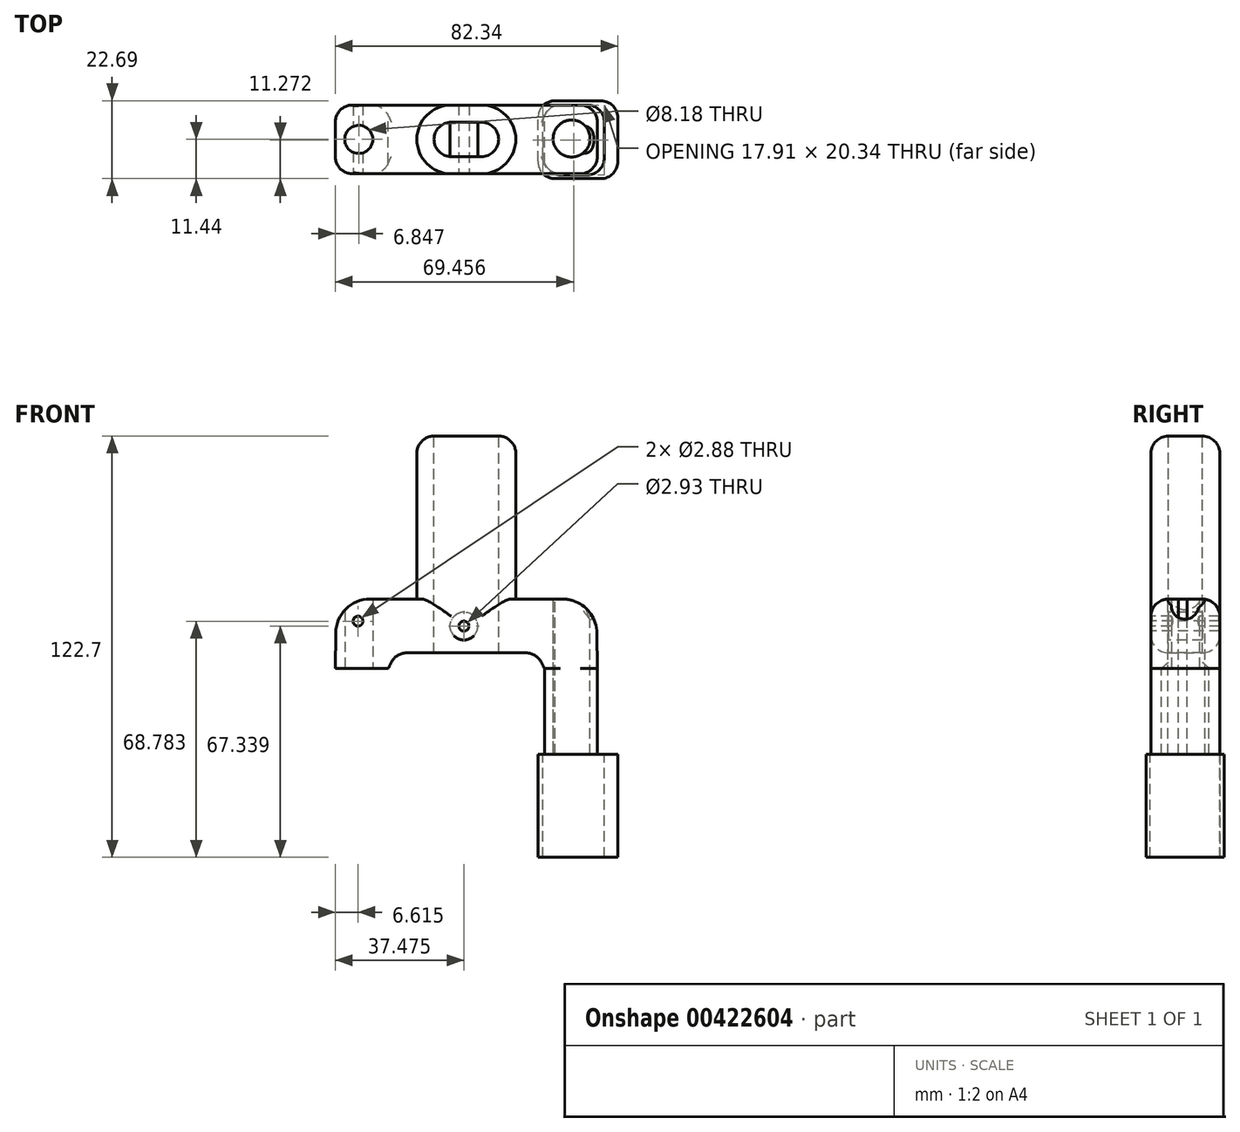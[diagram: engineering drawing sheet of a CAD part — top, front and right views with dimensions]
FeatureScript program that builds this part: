
annotation { "Feature Type Name" : "Feature", "Feature Type Description" : "" }
export const myFeature = defineFeature(function(context is Context, id is Id, definition is map)
    precondition{}
    {
        {
            var Q0;
            Q0=qCreatedBy(makeId("Front.planeOp"),FACE);
            var sketch = newSketch(context, id + "F0", { "sketchPlane" : qUnion([Q0])});
            skLineSegment(sketch, "E0", {"start": v(-67.5, -51.7) * mm, "end": v(-52.08, -51.7) * mm});
            skLineSegment(sketch, "E1", {"start": v(-52.08, -51.7) * mm, "end": v(-49.8, -47.15) * mm});
            skLineSegment(sketch, "E2", {"start": v(-49.8, -47.15) * mm, "end": v(-29.33, -47.15) * mm});
            skLineSegment(sketch, "E3", {"start": v(-29.33, -47.15) * mm, "end": v(-29.33, 0) * mm});
            skLineSegment(sketch, "E4", {"start": v(-29.33, 0) * mm, "end": v(-43.74, 0) * mm});
            skLineSegment(sketch, "E5", {"start": v(-43.74, 0) * mm, "end": v(-43.74, -31.47) * mm});
            skLineSegment(sketch, "E6", {"start": v(-43.74, -31.47) * mm, "end": v(-67.25, -31.47) * mm});
            skLineSegment(sketch, "E7", {"start": v(-67.25, -31.47) * mm, "end": v(-67.5, -51.7) * mm});
            skLineSegment(sketch, "E8.MirrorCS", {"start": v(-6.57, -51.7) * mm, "end": v(-8.85, -47.15) * mm});
            skLineSegment(sketch, "E9.MirrorCS", {"start": v(8.85, -51.7) * mm, "end": v(-6.57, -51.7) * mm});
            skLineSegment(sketch, "E10.MirrorCS", {"start": v(-14.92, -31.47) * mm, "end": v(8.6, -31.47) * mm});
            skLineSegment(sketch, "E11.MirrorCS", {"start": v(8.6, -31.47) * mm, "end": v(8.85, -51.7) * mm});
            skLineSegment(sketch, "E12.MirrorCS", {"start": v(-8.85, -47.15) * mm, "end": v(-29.33, -47.15) * mm});
            skLineSegment(sketch, "E13.MirrorCS", {"start": v(-29.33, 0) * mm, "end": v(-14.92, 0) * mm});
            skLineSegment(sketch, "E14.MirrorCS", {"start": v(-14.92, 0) * mm, "end": v(-14.92, -31.47) * mm});
            skSolve(sketch);
        }
        {
            var Q0;
            Q0=qSketchRegion(id+"F0",true);
            extrude(context, id + "F1", {"entities" : qUnion([Q0]), "depth" : 20 * mm});
        }
        {
            var Q0;
            Q0=makeQuery(id+"F1.opExtrude","SWEPT_EDGE",EDGE,{"disambiguationData":[OSD([sQuery(id+"F0.wireOp",EDGE,"E10.MirrorCS"),sQuery(id+"F0.wireOp",EDGE,"E11.MirrorCS")])]});
            var Q1;
            Q1=makeQuery(id+"F1.opExtrude","SWEPT_EDGE",EDGE,{"disambiguationData":[OSD([sQuery(id+"F0.wireOp",EDGE,"E6"),sQuery(id+"F0.wireOp",EDGE,"E7")])]});
            var Q2;
            Q2=makeQuery(id+"F1.opExtrude","CAP_EDGE",EDGE,{"disambiguationData":[OSD([sQuery(id+"F0.wireOp",EDGE,"E5")])],"isStart":false});
            var Q3;
            Q3=makeQuery(id+"F1.opExtrude","CAP_EDGE",EDGE,{"disambiguationData":[OSD([sQuery(id+"F0.wireOp",EDGE,"E14.MirrorCS")])],"isStart":false});
            var Q4;
            Q4=makeQuery(id+"F1.opExtrude","CAP_EDGE",EDGE,{"disambiguationData":[OSD([sQuery(id+"F0.wireOp",EDGE,"E5")])],"isStart":true});
            var Q5;
            Q5=makeQuery(id+"F1.opExtrude","CAP_EDGE",EDGE,{"disambiguationData":[OSD([sQuery(id+"F0.wireOp",EDGE,"E14.MirrorCS")])],"isStart":true});
            fillet(context, id + "F2", {"entities" : qUnion([Q0, Q1, Q2, Q3, Q4, Q5]), "radius" : 10 * mm, "tangentPropagation" : true, "allowEdgeOverflow" : false});
        }
        {
            var Q0;
            Q0=makeQuery(id+"F1.opExtrude","SWEPT_FACE",FACE,{"disambiguationData":[OSD([sQuery(id+"F0.wireOp",EDGE,"E4"),sQuery(id+"F0.wireOp",EDGE,"E13.MirrorCS")])]});
            extrude(context, id + "F3", {"entities" : qUnion([Q0]), "operationType" : NewBodyOperationType.ADD, "depth" : 16 * mm});
        }
        {
            var Q0;
            Q0=makeQuery(id+"F1.opExtrude","CAP_EDGE",EDGE,{"disambiguationData":[OSD([sQuery(id+"F0.wireOp",EDGE,"E11.MirrorCS")])],"isStart":false});
            var Q1;
            Q1=makeQuery(id+"F1.opExtrude","CAP_EDGE",EDGE,{"disambiguationData":[OSD([sQuery(id+"F0.wireOp",EDGE,"E6")])],"isStart":false});
            var Q2;
            {var subQ0=sQuery(id+"F0.wireOp",EDGE,"E7");var subQ1=sQuery(id+"F0.wireOp",EDGE,"E6");Q2=makeQuery(id+"F2.opFillet","BLEND_EDGE",EDGE,{"blendedFrom":[makeQuery(id+"F1.opExtrude","SWEPT_EDGE",EDGE,{"disambiguationData":[OSD([subQ1,subQ0])]}),makeQuery(id+"F1.opExtrude","CAP_FACE",FACE,{"disambiguationData":[OSD([sQuery(id+"F0.wireOp",EDGE,"E0"),sQuery(id+"F0.wireOp",EDGE,"E1"),sQuery(id+"F0.wireOp",EDGE,"E2"),sQuery(id+"F0.wireOp",EDGE,"E4"),sQuery(id+"F0.wireOp",EDGE,"E5"),subQ1,subQ0,sQuery(id+"F0.wireOp",EDGE,"E8.MirrorCS"),sQuery(id+"F0.wireOp",EDGE,"E9.MirrorCS"),sQuery(id+"F0.wireOp",EDGE,"E10.MirrorCS"),sQuery(id+"F0.wireOp",EDGE,"E11.MirrorCS"),sQuery(id+"F0.wireOp",EDGE,"E12.MirrorCS"),sQuery(id+"F0.wireOp",EDGE,"E13.MirrorCS"),sQuery(id+"F0.wireOp",EDGE,"E14.MirrorCS")])],"isStart":false})],"blendedInto":[makeQuery(id+"F1.opExtrude","CAP_FACE",FACE,{"disambiguationData":[OSD([sQuery(id+"F0.wireOp",EDGE,"E0"),sQuery(id+"F0.wireOp",EDGE,"E1"),sQuery(id+"F0.wireOp",EDGE,"E2"),sQuery(id+"F0.wireOp",EDGE,"E4"),sQuery(id+"F0.wireOp",EDGE,"E5"),subQ1,subQ0,sQuery(id+"F0.wireOp",EDGE,"E8.MirrorCS"),sQuery(id+"F0.wireOp",EDGE,"E9.MirrorCS"),sQuery(id+"F0.wireOp",EDGE,"E10.MirrorCS"),sQuery(id+"F0.wireOp",EDGE,"E11.MirrorCS"),sQuery(id+"F0.wireOp",EDGE,"E12.MirrorCS"),sQuery(id+"F0.wireOp",EDGE,"E13.MirrorCS"),sQuery(id+"F0.wireOp",EDGE,"E14.MirrorCS")])],"isStart":false})]});}
            var Q3;
            {var subQ0=sQuery(id+"F0.wireOp",EDGE,"E11.MirrorCS");var subQ1=sQuery(id+"F0.wireOp",EDGE,"E10.MirrorCS");Q3=makeQuery(id+"F2.opFillet","BLEND_EDGE",EDGE,{"blendedFrom":[makeQuery(id+"F1.opExtrude","SWEPT_EDGE",EDGE,{"disambiguationData":[OSD([subQ1,subQ0])]}),makeQuery(id+"F1.opExtrude","CAP_FACE",FACE,{"disambiguationData":[OSD([sQuery(id+"F0.wireOp",EDGE,"E0"),sQuery(id+"F0.wireOp",EDGE,"E1"),sQuery(id+"F0.wireOp",EDGE,"E2"),sQuery(id+"F0.wireOp",EDGE,"E4"),sQuery(id+"F0.wireOp",EDGE,"E5"),sQuery(id+"F0.wireOp",EDGE,"E6"),sQuery(id+"F0.wireOp",EDGE,"E7"),sQuery(id+"F0.wireOp",EDGE,"E8.MirrorCS"),sQuery(id+"F0.wireOp",EDGE,"E9.MirrorCS"),subQ1,subQ0,sQuery(id+"F0.wireOp",EDGE,"E12.MirrorCS"),sQuery(id+"F0.wireOp",EDGE,"E13.MirrorCS"),sQuery(id+"F0.wireOp",EDGE,"E14.MirrorCS")])],"isStart":true})],"blendedInto":[makeQuery(id+"F1.opExtrude","CAP_FACE",FACE,{"disambiguationData":[OSD([sQuery(id+"F0.wireOp",EDGE,"E0"),sQuery(id+"F0.wireOp",EDGE,"E1"),sQuery(id+"F0.wireOp",EDGE,"E2"),sQuery(id+"F0.wireOp",EDGE,"E4"),sQuery(id+"F0.wireOp",EDGE,"E5"),sQuery(id+"F0.wireOp",EDGE,"E6"),sQuery(id+"F0.wireOp",EDGE,"E7"),sQuery(id+"F0.wireOp",EDGE,"E8.MirrorCS"),sQuery(id+"F0.wireOp",EDGE,"E9.MirrorCS"),subQ1,subQ0,sQuery(id+"F0.wireOp",EDGE,"E12.MirrorCS"),sQuery(id+"F0.wireOp",EDGE,"E13.MirrorCS"),sQuery(id+"F0.wireOp",EDGE,"E14.MirrorCS")])],"isStart":true})]});}
            var Q4;
            {var subQ0=sQuery(id+"F0.wireOp",EDGE,"E7");var subQ1=sQuery(id+"F0.wireOp",EDGE,"E6");Q4=makeQuery(id+"F2.opFillet","BLEND_EDGE",EDGE,{"blendedFrom":[makeQuery(id+"F1.opExtrude","SWEPT_EDGE",EDGE,{"disambiguationData":[OSD([subQ1,subQ0])]}),makeQuery(id+"F1.opExtrude","CAP_FACE",FACE,{"disambiguationData":[OSD([sQuery(id+"F0.wireOp",EDGE,"E0"),sQuery(id+"F0.wireOp",EDGE,"E1"),sQuery(id+"F0.wireOp",EDGE,"E2"),sQuery(id+"F0.wireOp",EDGE,"E4"),sQuery(id+"F0.wireOp",EDGE,"E5"),subQ1,subQ0,sQuery(id+"F0.wireOp",EDGE,"E8.MirrorCS"),sQuery(id+"F0.wireOp",EDGE,"E9.MirrorCS"),sQuery(id+"F0.wireOp",EDGE,"E10.MirrorCS"),sQuery(id+"F0.wireOp",EDGE,"E11.MirrorCS"),sQuery(id+"F0.wireOp",EDGE,"E12.MirrorCS"),sQuery(id+"F0.wireOp",EDGE,"E13.MirrorCS"),sQuery(id+"F0.wireOp",EDGE,"E14.MirrorCS")])],"isStart":true})],"blendedInto":[makeQuery(id+"F1.opExtrude","CAP_FACE",FACE,{"disambiguationData":[OSD([sQuery(id+"F0.wireOp",EDGE,"E0"),sQuery(id+"F0.wireOp",EDGE,"E1"),sQuery(id+"F0.wireOp",EDGE,"E2"),sQuery(id+"F0.wireOp",EDGE,"E4"),sQuery(id+"F0.wireOp",EDGE,"E5"),subQ1,subQ0,sQuery(id+"F0.wireOp",EDGE,"E8.MirrorCS"),sQuery(id+"F0.wireOp",EDGE,"E9.MirrorCS"),sQuery(id+"F0.wireOp",EDGE,"E10.MirrorCS"),sQuery(id+"F0.wireOp",EDGE,"E11.MirrorCS"),sQuery(id+"F0.wireOp",EDGE,"E12.MirrorCS"),sQuery(id+"F0.wireOp",EDGE,"E13.MirrorCS"),sQuery(id+"F0.wireOp",EDGE,"E14.MirrorCS")])],"isStart":true})]});}
            var Q5;
            Q5=makeQuery(id+"F3.opExtrude","CAP_EDGE",EDGE,{"disambiguationData":[OSD([sQuery(id+"F0.wireOp",EDGE,"E4"),sQuery(id+"F0.wireOp",EDGE,"E13.MirrorCS"),sQuery(id+"F0.wireOp",EDGE,"E14.MirrorCS")])],"isStart":false});
            var Q6;
            Q6=makeQuery(id+"F3.opExtrude","CAP_EDGE",EDGE,{"disambiguationData":[OSD([sQuery(id+"F0.wireOp",EDGE,"E4"),sQuery(id+"F0.wireOp",EDGE,"E5"),sQuery(id+"F0.wireOp",EDGE,"E13.MirrorCS")])],"isStart":false});
            var Q7;
            {var subQ0=sQuery(id+"F0.wireOp",EDGE,"E13.MirrorCS");var subQ1=sQuery(id+"F0.wireOp",EDGE,"E4");Q7=makeQuery(id+"F3.opExtrude","CAP_EDGE",EDGE,{"disambiguationData":[OSD([subQ1,subQ0]),TDD([makeQuery(id+"F1.opExtrude","CAP_EDGE",EDGE,{"disambiguationData":[OSD([subQ1,subQ0])],"isStart":false})])],"isStart":false});}
            fillet(context, id + "F4", {"entities" : qUnion([Q0, Q1, Q2, Q3, Q4, Q5, Q6, Q7]), "radius" : 5 * mm, "tangentPropagation" : true, "allowEdgeOverflow" : false});
        }
        {
            var Q0;
            Q0=makeQuery(id+"F1.opExtrude","SWEPT_FACE",FACE,{"disambiguationData":[OSD([sQuery(id+"F0.wireOp",EDGE,"E2"),sQuery(id+"F0.wireOp",EDGE,"E12.MirrorCS")])]});
            fillet(context, id + "F5", {"entities" : qUnion([Q0]), "radius" : 5 * mm, "tangentPropagation" : true, "allowEdgeOverflow" : false});
        }
        {
            var Q0;
            Q0=makeQuery(id+"F3.opExtrude","CAP_FACE",FACE,{"disambiguationData":[OSD([sQuery(id+"F0.wireOp",EDGE,"E4"),sQuery(id+"F0.wireOp",EDGE,"E13.MirrorCS")])],"isStart":false});
            extrude(context, id + "F6", {"entities" : qUnion([Q0]), "operationType" : NewBodyOperationType.REMOVE, "oppositeDirection" : true, "depth" : 89 * mm});
        }
        {
            var Q0;
            Q0=makeQuery(id+"F1.opExtrude","SWEPT_FACE",FACE,{"disambiguationData":[OSD([sQuery(id+"F0.wireOp",EDGE,"E0")])]});
            var sketch = newSketch(context, id + "F7", { "sketchPlane" : qUnion([Q0])});
            skCircle(sketch, "E15", {"center": v(-60.65, 10) * mm, "radius": 4.09 * mm});
            skPoint(sketch, "E15.centerSnap0", {"position": v(-57.67, 10) * mm});
            skSolve(sketch);
        }
        {
            var Q0;
            Q0=makeQuery(id+"F7.imprint","IMPRINT",FACE,{"disambiguationData":[TD([[makeQuery(id+"F7.imprint","IMPRINT",EDGE,{"derivedFrom":sQuery(id+"F7.wireOp",EDGE,"E15")}),1.0]])]});
            var Q1;
            Q1=sQuery(id+"F7.wireOp",EDGE,"E15");
            extrude(context, id + "F8", {"entities" : qUnion([Q0]), "operationType" : NewBodyOperationType.REMOVE, "surfaceEntities" : qUnion([Q1]), "oppositeDirection" : true, "depth" : 25 * mm});
        }
        {
            var Q0;
            Q0=makeQuery(id+"F1.opExtrude","SWEPT_FACE",FACE,{"disambiguationData":[OSD([sQuery(id+"F0.wireOp",EDGE,"E9.MirrorCS")])]});
            var sketch = newSketch(context, id + "F9", { "sketchPlane" : qUnion([Q0])});
            skCircle(sketch, "E16", {"center": v(0, 10) * mm, "radius": 4.07 * mm});
            skPoint(sketch, "E16.centerSnap0", {"position": v(3.85, 10) * mm});
            skSolve(sketch);
        }
        {
            var Q0;
            Q0=makeQuery(id+"F9.imprint","IMPRINT",FACE,{"disambiguationData":[TD([[makeQuery(id+"F9.imprint","IMPRINT",EDGE,{"derivedFrom":sQuery(id+"F9.wireOp",EDGE,"E16")}),1.0]])]});
            extrude(context, id + "F10", {"entities" : qUnion([Q0]), "operationType" : NewBodyOperationType.REMOVE, "oppositeDirection" : true, "depth" : 25 * mm});
        }
        {
            var Q0;
            Q0=makeQuery(id+"F1.opExtrude","SWEPT_FACE",FACE,{"disambiguationData":[OSD([sQuery(id+"F0.wireOp",EDGE,"E9.MirrorCS")])]});
            extrude(context, id + "F11", {"entities" : qUnion([Q0]), "operationType" : NewBodyOperationType.ADD, "depth" : 25 * mm});
        }
        {
            var Q0;
            Q0=makeQuery(id+"F1.opExtrude","SWEPT_FACE",FACE,{"disambiguationData":[OSD([sQuery(id+"F0.wireOp",EDGE,"E11.MirrorCS")])]});
            var sketch = newSketch(context, id + "F12", { "sketchPlane" : qUnion([Q0])});
            skCircle(sketch, "E17", {"center": v(-10.12, -33.44) * mm, "radius": 3.97 * mm});
            skSolve(sketch);
        }
        {
            var Q0;
            Q0=qSketchRegion(id+"F12",true);
            extrude(context, id + "F13", {"entities" : qUnion([Q0]), "operationType" : NewBodyOperationType.REMOVE, "oppositeDirection" : true, "depth" : 9 * mm});
        }
        {
            var Q0;
            Q0=qCreatedBy(makeId("Top.planeOp"),FACE);
            var sketch = newSketch(context, id + "F14", { "sketchPlane" : qUnion([Q0])});
            skCircle(sketch, "E18", {"center": v(1.35, -9.73) * mm, "radius": 5.39 * mm});
            skSolve(sketch);
        }
        {
            var Q0;
            Q0=qSketchRegion(id+"F14",true);
            extrude(context, id + "F15", {"entities" : qUnion([Q0]), "operationType" : NewBodyOperationType.REMOVE, "oppositeDirection" : true, "depth" : 100 * mm});
        }
        {
            var Q0;
            {var subQ0=sQuery(id+"F0.wireOp",EDGE,"E9.MirrorCS");var subQ1=sQuery(id+"F0.wireOp",EDGE,"E13.MirrorCS");var subQ2=sQuery(id+"F0.wireOp",EDGE,"E4");Q0=makeQuery(id+"F11.boolean.opBoolean","MERGE",FACE,{"derivedFrom":[makeQuery(id+"F3.boolean.opBoolean","MERGE",FACE,{"derivedFrom":[makeQuery(id+"F1.opExtrude","CAP_FACE",FACE,{"disambiguationData":[OSD([sQuery(id+"F0.wireOp",EDGE,"E0"),sQuery(id+"F0.wireOp",EDGE,"E1"),sQuery(id+"F0.wireOp",EDGE,"E2"),subQ2,sQuery(id+"F0.wireOp",EDGE,"E5"),sQuery(id+"F0.wireOp",EDGE,"E6"),sQuery(id+"F0.wireOp",EDGE,"E7"),sQuery(id+"F0.wireOp",EDGE,"E8.MirrorCS"),subQ0,sQuery(id+"F0.wireOp",EDGE,"E10.MirrorCS"),sQuery(id+"F0.wireOp",EDGE,"E11.MirrorCS"),sQuery(id+"F0.wireOp",EDGE,"E12.MirrorCS"),subQ1,sQuery(id+"F0.wireOp",EDGE,"E14.MirrorCS")])],"isStart":false}),makeQuery(id+"F3.opExtrude","SWEPT_FACE",FACE,{"disambiguationData":[OSD([subQ2,subQ1]),TDD([makeQuery(id+"F1.opExtrude","CAP_EDGE",EDGE,{"disambiguationData":[OSD([subQ2,subQ1])],"isStart":false})])]})]}),makeQuery(id+"F11.opExtrude","SWEPT_FACE",FACE,{"disambiguationData":[OSD([subQ0]),TDD([makeQuery(id+"F1.opExtrude","CAP_EDGE",EDGE,{"disambiguationData":[OSD([subQ0])],"isStart":false})])]})]});}
            var sketch = newSketch(context, id + "F16", { "sketchPlane" : qUnion([Q0])});
            skCircle(sketch, "E19", {"center": v(-60.88, -37.92) * mm, "radius": 1.44 * mm});
            skSolve(sketch);
        }
        {
            var Q0;
            Q0=qSketchRegion(id+"F16",true);
            extrude(context, id + "F17", {"entities" : qUnion([Q0]), "operationType" : NewBodyOperationType.REMOVE, "oppositeDirection" : true, "depth" : 25 * mm});
        }
        {
            var Q0;
            {var subQ0=sQuery(id+"F0.wireOp",EDGE,"E9.MirrorCS");var subQ1=sQuery(id+"F0.wireOp",EDGE,"E13.MirrorCS");var subQ2=sQuery(id+"F0.wireOp",EDGE,"E4");Q0=makeQuery(id+"F11.boolean.opBoolean","MERGE",FACE,{"derivedFrom":[makeQuery(id+"F3.boolean.opBoolean","MERGE",FACE,{"derivedFrom":[makeQuery(id+"F1.opExtrude","CAP_FACE",FACE,{"disambiguationData":[OSD([sQuery(id+"F0.wireOp",EDGE,"E0"),sQuery(id+"F0.wireOp",EDGE,"E1"),sQuery(id+"F0.wireOp",EDGE,"E2"),subQ2,sQuery(id+"F0.wireOp",EDGE,"E5"),sQuery(id+"F0.wireOp",EDGE,"E6"),sQuery(id+"F0.wireOp",EDGE,"E7"),sQuery(id+"F0.wireOp",EDGE,"E8.MirrorCS"),subQ0,sQuery(id+"F0.wireOp",EDGE,"E10.MirrorCS"),sQuery(id+"F0.wireOp",EDGE,"E11.MirrorCS"),sQuery(id+"F0.wireOp",EDGE,"E12.MirrorCS"),subQ1,sQuery(id+"F0.wireOp",EDGE,"E14.MirrorCS")])],"isStart":false}),makeQuery(id+"F3.opExtrude","SWEPT_FACE",FACE,{"disambiguationData":[OSD([subQ2,subQ1]),TDD([makeQuery(id+"F1.opExtrude","CAP_EDGE",EDGE,{"disambiguationData":[OSD([subQ2,subQ1])],"isStart":false})])]})]}),makeQuery(id+"F11.opExtrude","SWEPT_FACE",FACE,{"disambiguationData":[OSD([subQ0]),TDD([makeQuery(id+"F1.opExtrude","CAP_EDGE",EDGE,{"disambiguationData":[OSD([subQ0])],"isStart":false})])]})]});}
            var sketch = newSketch(context, id + "F18", { "sketchPlane" : qUnion([Q0])});
            skCircle(sketch, "E20", {"center": v(-30.03, -39.36) * mm, "radius": 4.04 * mm});
            skSolve(sketch);
        }
        {
            var Q0;
            Q0=qSketchRegion(id+"F18",true);
            extrude(context, id + "F19", {"entities" : qUnion([Q0]), "operationType" : NewBodyOperationType.ADD, "oppositeDirection" : true, "depth" : 20 * mm});
        }
        {
            var Q0;
            {var subQ0=sQuery(id+"F0.wireOp",EDGE,"E9.MirrorCS");var subQ1=sQuery(id+"F0.wireOp",EDGE,"E13.MirrorCS");var subQ2=sQuery(id+"F0.wireOp",EDGE,"E4");Q0=makeQuery(id+"F19.boolean.opBoolean","MERGE",FACE,{"derivedFrom":[makeQuery(id+"F11.boolean.opBoolean","MERGE",FACE,{"derivedFrom":[makeQuery(id+"F3.boolean.opBoolean","MERGE",FACE,{"derivedFrom":[makeQuery(id+"F1.opExtrude","CAP_FACE",FACE,{"disambiguationData":[OSD([sQuery(id+"F0.wireOp",EDGE,"E0"),sQuery(id+"F0.wireOp",EDGE,"E1"),sQuery(id+"F0.wireOp",EDGE,"E2"),subQ2,sQuery(id+"F0.wireOp",EDGE,"E5"),sQuery(id+"F0.wireOp",EDGE,"E6"),sQuery(id+"F0.wireOp",EDGE,"E7"),sQuery(id+"F0.wireOp",EDGE,"E8.MirrorCS"),subQ0,sQuery(id+"F0.wireOp",EDGE,"E10.MirrorCS"),sQuery(id+"F0.wireOp",EDGE,"E11.MirrorCS"),sQuery(id+"F0.wireOp",EDGE,"E12.MirrorCS"),subQ1,sQuery(id+"F0.wireOp",EDGE,"E14.MirrorCS")])],"isStart":false}),makeQuery(id+"F3.opExtrude","SWEPT_FACE",FACE,{"disambiguationData":[OSD([subQ2,subQ1]),TDD([makeQuery(id+"F1.opExtrude","CAP_EDGE",EDGE,{"disambiguationData":[OSD([subQ2,subQ1])],"isStart":false})])]})]}),makeQuery(id+"F11.opExtrude","SWEPT_FACE",FACE,{"disambiguationData":[OSD([subQ0]),TDD([makeQuery(id+"F1.opExtrude","CAP_EDGE",EDGE,{"disambiguationData":[OSD([subQ0])],"isStart":false})])]})]}),makeQuery(id+"F19.opExtrude","CAP_FACE",FACE,{"disambiguationData":[OSD([sQuery(id+"F18.wireOp",EDGE,"E20")])],"isStart":true})]});}
            var sketch = newSketch(context, id + "F20", { "sketchPlane" : qUnion([Q0])});
            skCircle(sketch, "E21", {"center": v(-30.03, -39.36) * mm, "radius": 1.47 * mm});
            skSolve(sketch);
        }
        {
            var Q0;
            Q0=qSketchRegion(id+"F20",true);
            extrude(context, id + "F21", {"entities" : qUnion([Q0]), "operationType" : NewBodyOperationType.REMOVE, "oppositeDirection" : true, "depth" : 25 * mm});
        }
        {
            var Q0;
            Q0=makeQuery(id+"F11.opExtrude","CAP_FACE",FACE,{"disambiguationData":[OSD([sQuery(id+"F0.wireOp",EDGE,"E9.MirrorCS")])],"isStart":false});
            var sketch = newSketch(context, id + "F22", { "sketchPlane" : qUnion([Q0])});
            skLineSegment(sketch, "E22.bottom", {"start": v(5.91, 20.34) * mm, "end": v(-2, 20.34) * mm});
            skLineSegment(sketch, "E22.top", {"start": v(5.91, 0) * mm, "end": v(-2, 0) * mm});
            skLineSegment(sketch, "E22.left", {"start": v(10.91, 15.34) * mm, "end": v(10.91, 5) * mm});
            skLineSegment(sketch, "E22.right", {"start": v(-7, 15.34) * mm, "end": v(-7, 5) * mm});
            skPoint(sketch, "E23.visualSharp", {"position": v(10.91, 20.34) * mm});
            skArc(sketch, "E23.filletArc", {"start": v(10.91, 15.34) * mm, "mid": v(9.45, 18.87) * mm, "end": v(5.91, 20.34) * mm});
            skPoint(sketch, "E24.visualSharp", {"position": v(-7, 20.34) * mm});
            skArc(sketch, "E24.filletArc", {"start": v(-2, 20.34) * mm, "mid": v(-5.54, 18.87) * mm, "end": v(-7, 15.34) * mm});
            skPoint(sketch, "E25.visualSharp", {"position": v(-7, 0) * mm});
            skArc(sketch, "E25.filletArc", {"start": v(-7, 5) * mm, "mid": v(-5.54, 1.46) * mm, "end": v(-2, 0) * mm});
            skPoint(sketch, "E26.visualSharp", {"position": v(10.91, 0) * mm});
            skArc(sketch, "E26.filletArc", {"start": v(5.91, 0) * mm, "mid": v(9.45, 1.46) * mm, "end": v(10.91, 5) * mm});
            skLineSegment(sketch, "E27.bottom", {"start": v(-3.46, 21.44) * mm, "end": v(9.84, 21.44) * mm});
            skLineSegment(sketch, "E27.top", {"start": v(-3.46, -1.25) * mm, "end": v(9.84, -1.25) * mm});
            skLineSegment(sketch, "E27.left", {"start": v(-8.46, 16.44) * mm, "end": v(-8.46, 3.75) * mm});
            skLineSegment(sketch, "E27.right", {"start": v(14.84, 16.44) * mm, "end": v(14.84, 3.75) * mm});
            skPoint(sketch, "E28.visualSharp", {"position": v(-8.46, 21.44) * mm});
            skArc(sketch, "E28.filletArc", {"start": v(-3.46, 21.44) * mm, "mid": v(-7, 19.97) * mm, "end": v(-8.46, 16.44) * mm});
            skPoint(sketch, "E29.visualSharp", {"position": v(14.84, 21.44) * mm});
            skArc(sketch, "E29.filletArc", {"start": v(14.84, 16.44) * mm, "mid": v(13.37, 19.97) * mm, "end": v(9.84, 21.44) * mm});
            skPoint(sketch, "E30.visualSharp", {"position": v(14.84, -1.25) * mm});
            skArc(sketch, "E30.filletArc", {"start": v(9.84, -1.25) * mm, "mid": v(13.37, 0.22) * mm, "end": v(14.84, 3.75) * mm});
            skPoint(sketch, "E31.visualSharp", {"position": v(-8.46, -1.25) * mm});
            skArc(sketch, "E31.filletArc", {"start": v(-8.46, 3.75) * mm, "mid": v(-7, 0.22) * mm, "end": v(-3.46, -1.25) * mm});
            skSolve(sketch);
        }
        {
            var Q0;
            Q0 = qSketchRegion(id + "F22", true);
            extrude(context, id + "F23", {"entities" : qUnion([Q0]), "operationType" : NewBodyOperationType.ADD, "depth" : 30 * mm});
        }
    });
